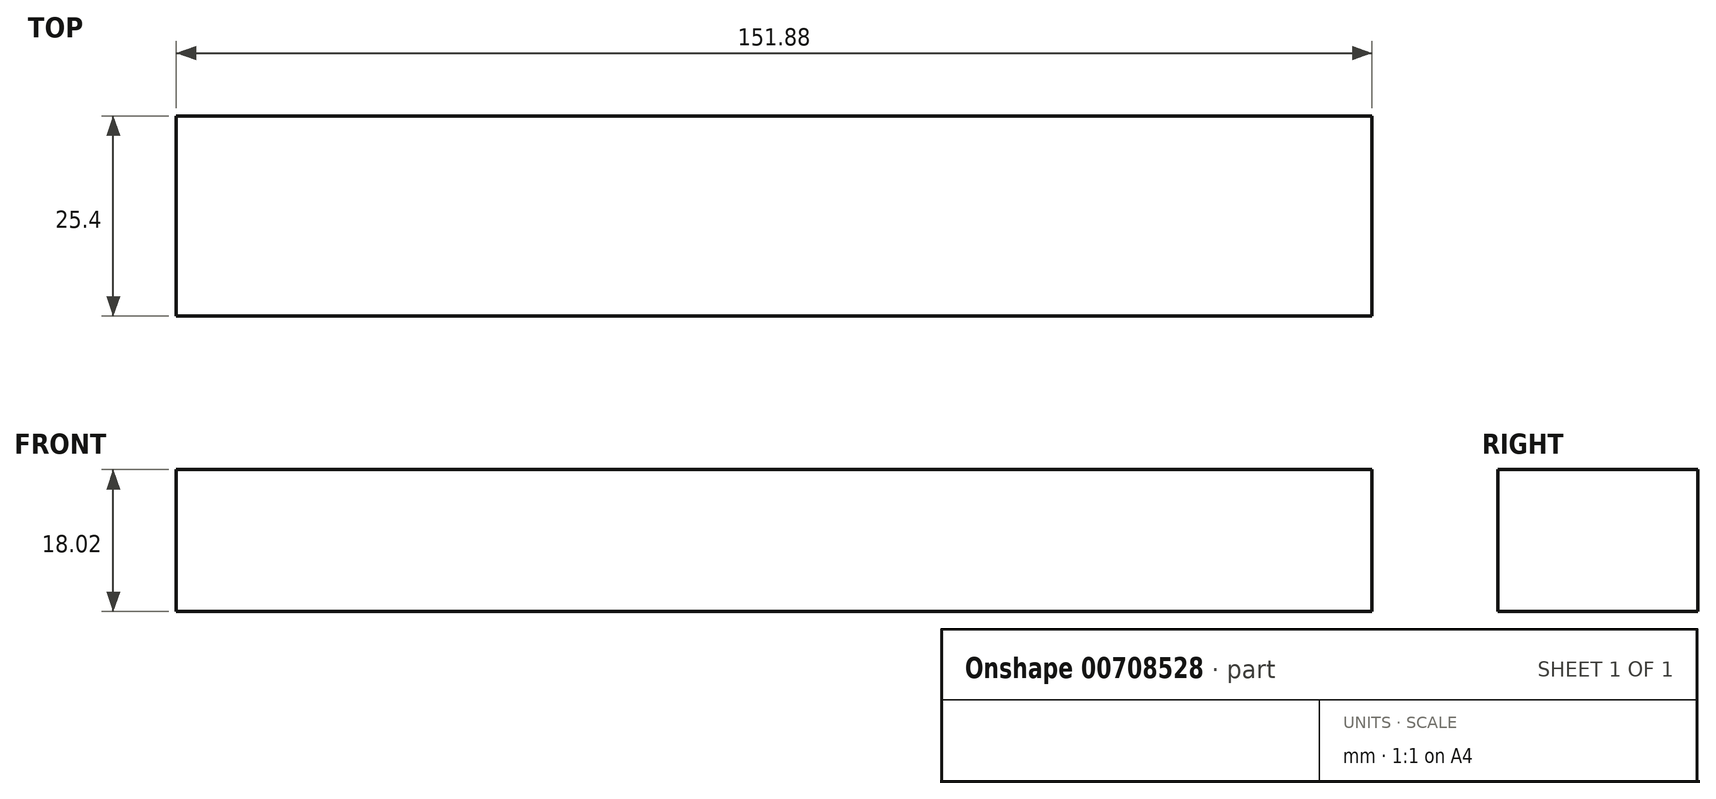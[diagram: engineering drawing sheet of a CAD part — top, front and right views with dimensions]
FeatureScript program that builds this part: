
annotation { "Feature Type Name" : "Feature", "Feature Type Description" : "" }
export const myFeature = defineFeature(function(context is Context, id is Id, definition is map)
    precondition{}
    {
        {
            var Q0;
            Q0=qCreatedBy(makeId("Front.planeOp"),FACE);
            var sketch = newSketch(context, id + "F0", { "sketchPlane" : qUnion([Q0])});
            skLineSegment(sketch, "E0.bottom", {"start": v(-75.94, 11.58) * mm, "end": v(75.94, 11.58) * mm});
            skLineSegment(sketch, "E0.top", {"start": v(-75.94, -6.44) * mm, "end": v(75.94, -6.44) * mm});
            skLineSegment(sketch, "E0.left", {"start": v(-75.94, 11.58) * mm, "end": v(-75.94, -6.44) * mm});
            skLineSegment(sketch, "E0.right", {"start": v(75.94, 11.58) * mm, "end": v(75.94, -6.44) * mm});
            skSolve(sketch);
        }
        {
            var Q0;
            Q0=sQuery(id+"F0.wireOp",EDGE,"E0.left");
            var Q1;
            Q1=sQuery(id+"F0.wireOp",EDGE,"E0.right");
            var Q2;
            Q2=sQuery(id+"F0.wireOp",EDGE,"E0.top");
            var Q3;
            Q3=sQuery(id+"F0.wireOp",EDGE,"E0.bottom");
            extrude(context, id + "F1", {"bodyType" : ToolBodyType.SURFACE, "operationType" : NewBodyOperationType.ADD, "surfaceEntities" : qUnion([Q0, Q1, Q2, Q3]), "depth" : 25.4 * mm, "offsetDistance" : 25.4 * mm});
        }
    });
